MODEL slx_410938a03b86
CONFIG AbsTol = auto
CONFIG EnableMultiTasking = off
CONFIG FixedStep = auto
CONFIG MaxStep = auto
CONFIG MinStep = auto
CONFIG RelTol = 1e-3
CONFIG SampleTimeConstraint = Unconstrained
CONFIG SolverName = ode23s
CONFIG StartTime = 0.0
CONFIG StopTime = 173
BLOCK [Constant] Constant
  Value = max_torque_req
BLOCK [Constant] Constant1
  Value = 0.013
BLOCK [Constant] Constant2
  Value = 0.013
BLOCK [Constant] Constant3
  Value = max_torque_req
BLOCK [FromWorkspace] From Workspace
  VariableName = steering_ang
BLOCK [FromWorkspace] From Workspace2
  VariableName = steering_ang
BLOCK [Gain] Gain
  Gain = 1/M
BLOCK [Gain] Gain1
  Gain = M/4*g
  NameLocation = right
BLOCK [Gain] Gain2
  Gain = M/4*g
  NameLocation = right
BLOCK [Gain] Gain3
  Gain = 8.5/(M/2)
BLOCK [Gain] Gain4
  Gain = 8.5/(M/2)
BLOCK [FromWorkspace] LeftMotorTemp
  VariableName = left_mtr_tmp
BLOCK [SubSystem] MATLAB Function1
  ErrorFcn = Stateflow.Translate.translate
  PermitHierarchicalResolution = ExplicitOnly
  SFBlockType = MATLAB Function
  TreatAsAtomicUnit = on
BLOCK [Demux] MATLAB Function1/ Demux 
  Outputs = 1
BLOCK [S-Function] MATLAB Function1/ SFunction 
  EnableBusSupport = on
  FunctionName = sf_sfun
  PortCounts = [2 2]
  SFcnIsStateOwnerBlock = off
  SFunctionDeploymentMode = off
  Tag = Stateflow S-Function 12
BLOCK [Terminator] MATLAB Function1/ Terminator 
BLOCK [Outport] MATLAB Function1/frr
BLOCK [Inport] MATLAB Function1/prev_wheel_ang_vel
BLOCK [Inport] MATLAB Function1/rolling_coeff
  Port = 2
BLOCK [SubSystem] MATLAB Function2
  ErrorFcn = Stateflow.Translate.translate
  PermitHierarchicalResolution = ExplicitOnly
  SFBlockType = MATLAB Function
  TreatAsAtomicUnit = on
BLOCK [Demux] MATLAB Function2/ Demux 
  Outputs = 1
BLOCK [S-Function] MATLAB Function2/ SFunction 
  EnableBusSupport = on
  FunctionName = sf_sfun
  PortCounts = [2 2]
  SFcnIsStateOwnerBlock = off
  SFunctionDeploymentMode = off
  Tag = Stateflow S-Function 13
BLOCK [Terminator] MATLAB Function2/ Terminator 
BLOCK [Outport] MATLAB Function2/frr
BLOCK [Inport] MATLAB Function2/prev_wheel_ang_vel
BLOCK [Inport] MATLAB Function2/rolling_coeff
  Port = 2
BLOCK [Memory] Memory
BLOCK [Memory] Memory1
BLOCK [Memory] Memory3
  NameLocation = right
BLOCK [FromWorkspace] PedalPercent
  VariableName = pdl_percent
BLOCK [FromWorkspace] PedalPercent1
  VariableName = pdl_percent
BLOCK [SubSystem] Pedal_Based_Torque_Mapping
  ErrorFcn = Stateflow.Translate.translate
  PermitHierarchicalResolution = ExplicitOnly
  SFBlockType = MATLAB Function
  TreatAsAtomicUnit = on
BLOCK [Demux] Pedal_Based_Torque_Mapping/ Demux 
  Outputs = 1
BLOCK [S-Function] Pedal_Based_Torque_Mapping/ SFunction 
  EnableBusSupport = on
  FunctionName = sf_sfun
  PortCounts = [3 3]
  SFcnIsStateOwnerBlock = off
  SFunctionDeploymentMode = off
  Tag = Stateflow S-Function 8
BLOCK [Terminator] Pedal_Based_Torque_Mapping/ Terminator 
BLOCK [Outport] Pedal_Based_Torque_Mapping/T_req_active_diff
BLOCK [Outport] Pedal_Based_Torque_Mapping/T_req_slip_control
  Port = 2
BLOCK [Inport] Pedal_Based_Torque_Mapping/max_torque_req
BLOCK [Inport] Pedal_Based_Torque_Mapping/p_a
  Port = 3
BLOCK [Inport] Pedal_Based_Torque_Mapping/steering_angle
  Port = 2
BLOCK [Product] Product
BLOCK [FromWorkspace] RightMotorTemp
  VariableName = right_mtr_tmp
BLOCK [Scope] Scope
  Floating = off
  NumInputPorts = 1
  ScopeSpecificationString = Simulink.scopes.TimeScopeBlockCfg('CurrentConfiguration', extmgr.ConfigurationSet(extmgr.Configuration('Core','General UI',true),extmgr.Configuration('Core','Source UI',true),extmgr.Configuration('Sources','WiredSimulink',true,'DataLoggingVariableName','ScopeData1'),extmgr.Configuration('Visuals','Time Domain',true,'SerializedDisplays',{struct('MinYLimReal','-128.05151','MaxYLimReal','52.46356','Y...<+1474ch>
BLOCK [Sum] Sum
  Inputs = |+-
BLOCK [Sum] Sum1
  Inputs = |-+
BLOCK [Sum] Sum2
  Inputs = |++
BLOCK [Sum] Sum4
  Inputs = |+-
BLOCK [Sum] Sum5
  Inputs = |++
BLOCK [SubSystem] activeDiff
BLOCK [Constant] activeDiff/Constant
BLOCK [SubSystem] activeDiff/MATLAB Function
  ErrorFcn = Stateflow.Translate.translate
  PermitHierarchicalResolution = ExplicitOnly
  SFBlockType = MATLAB Function
  TreatAsAtomicUnit = on
BLOCK [Demux] activeDiff/MATLAB Function/ Demux 
  Outputs = 1
BLOCK [S-Function] activeDiff/MATLAB Function/ SFunction 
  EnableBusSupport = on
  FunctionName = sf_sfun
  PortCounts = [3 2]
  SFcnIsStateOwnerBlock = off
  SFunctionDeploymentMode = off
  Tag = Stateflow S-Function 9
BLOCK [Terminator] activeDiff/MATLAB Function/ Terminator 
BLOCK [Inport] activeDiff/MATLAB Function/conversion_factor
  Port = 2
BLOCK [Inport] activeDiff/MATLAB Function/inverter_power
BLOCK [Outport] activeDiff/MATLAB Function/motor_RPM
BLOCK [Inport] activeDiff/MATLAB Function/torque_request
  Port = 3
BLOCK [Inport] activeDiff/Pedal Torque
  Port = 3
BLOCK [Inport] activeDiff/Power Limit
  Port = 2
BLOCK [SubSystem] activeDiff/Power_to_torque
  ErrorFcn = Stateflow.Translate.translate
  PermitHierarchicalResolution = ExplicitOnly
  SFBlockType = MATLAB Function
  TreatAsAtomicUnit = on
BLOCK [Demux] activeDiff/Power_to_torque/ Demux 
  Outputs = 1
BLOCK [S-Function] activeDiff/Power_to_torque/ SFunction 
  EnableBusSupport = on
  FunctionName = sf_sfun
  PortCounts = [6 2]
  SFcnIsStateOwnerBlock = off
  SFunctionDeploymentMode = off
  Tag = Stateflow S-Function 7
BLOCK [Terminator] activeDiff/Power_to_torque/ Terminator 
BLOCK [Inport] activeDiff/Power_to_torque/cl
  Port = 4
BLOCK [Inport] activeDiff/Power_to_torque/cr
  Port = 5
BLOCK [Inport] activeDiff/Power_to_torque/left_motor_speed
BLOCK [Outport] activeDiff/Power_to_torque/max_power_to_torque
BLOCK [Inport] activeDiff/Power_to_torque/p_to_t_conversion_factor
  Port = 6
BLOCK [Inport] activeDiff/Power_to_torque/power_KW_input
  Port = 3
BLOCK [Inport] activeDiff/Power_to_torque/right_motor_speed
  Port = 2
BLOCK [Inport] activeDiff/Steering Angle
BLOCK [SubSystem] activeDiff/Steering_Angle_To_Delta
  ErrorFcn = Stateflow.Translate.translate
  PermitHierarchicalResolution = ExplicitOnly
  SFBlockType = MATLAB Function
  TreatAsAtomicUnit = on
BLOCK [Demux] activeDiff/Steering_Angle_To_Delta/ Demux 
  Outputs = 1
BLOCK [S-Function] activeDiff/Steering_Angle_To_Delta/ SFunction 
  EnableBusSupport = on
  FunctionName = sf_sfun
  PortCounts = [3 2]
  SFcnIsStateOwnerBlock = off
  SFunctionDeploymentMode = off
  Tag = Stateflow S-Function 6
BLOCK [Terminator] activeDiff/Steering_Angle_To_Delta/ Terminator 
BLOCK [Inport] activeDiff/Steering_Angle_To_Delta/TRACK_WIDTH_mm
  Port = 2
BLOCK [Inport] activeDiff/Steering_Angle_To_Delta/WHEELBASE_mm
  Port = 3
BLOCK [Outport] activeDiff/Steering_Angle_To_Delta/delta
BLOCK [Inport] activeDiff/Steering_Angle_To_Delta/wheel_angle_deg
BLOCK [Sum] activeDiff/Sum
  Inputs = |++
BLOCK [Sum] activeDiff/Sum1
  Inputs = |+-
BLOCK [Constant] activeDiff/Track_width_mm
  Value = 1100
BLOCK [Constant] activeDiff/Track_width_mm1
  Value = 1550
BLOCK [Constant] activeDiff/conversion_factor
  Value = 9550
BLOCK [Outport] activeDiff/left_active_diff_torque
  Port = 3
BLOCK [Outport] activeDiff/max_power_to_torque
BLOCK [Outport] activeDiff/right_active_diff_torque
  Port = 2
BLOCK [SubSystem] activeDiff/torque_to_send
  ErrorFcn = Stateflow.Translate.translate
  PermitHierarchicalResolution = ExplicitOnly
  SFBlockType = MATLAB Function
  TreatAsAtomicUnit = on
BLOCK [Demux] activeDiff/torque_to_send/ Demux 
  Outputs = 1
BLOCK [S-Function] activeDiff/torque_to_send/ SFunction 
  EnableBusSupport = on
  FunctionName = sf_sfun
  PortCounts = [4 3]
  SFcnIsStateOwnerBlock = off
  SFunctionDeploymentMode = off
  Tag = Stateflow S-Function 5
BLOCK [Terminator] activeDiff/torque_to_send/ Terminator 
BLOCK [Inport] activeDiff/torque_to_send/cl
BLOCK [Inport] activeDiff/torque_to_send/cr
  Port = 2
BLOCK [Outport] activeDiff/torque_to_send/left_computed_torque
BLOCK [Inport] activeDiff/torque_to_send/request_torque
  Port = 3
BLOCK [Outport] activeDiff/torque_to_send/right_computed_torque
  Port = 2
BLOCK [Inport] activeDiff/torque_to_send/torque_lim
  Port = 4
BLOCK [MinMax] clamp1
  Function = max
  Inputs = 2
BLOCK [MinMax] clamp2
  Inputs = 2
BLOCK [MinMax] clamp3
  Function = max
  Inputs = 2
BLOCK [MinMax] clamp4
  Inputs = 2
BLOCK [Gain] drag_f_form
  Gain = 0.5* mass_den * Cd * Af
BLOCK [SubSystem] left_tire_model
BLOCK [Constant] left_tire_model/Constant
  Value = 0
BLOCK [Outport] left_tire_model/F_x_L
  Port = 2
BLOCK [From] left_tire_model/From
  GotoTag = vehicle_v_x
  NameLocation = top
BLOCK [From] left_tire_model/From F_x
  GotoTag = F_x
BLOCK [FromWorkspace] left_tire_model/From Workspace
  SampleTime = -1
  VariableName = recorded_vel
BLOCK [From] left_tire_model/From1
  GotoTag = vehicle_a_x
  NameLocation = top
BLOCK [From] left_tire_model/From2
  GotoTag = slip_ratio
BLOCK [From] left_tire_model/From3
  GotoTag = wheel_ang_v_x
BLOCK [From] left_tire_model/From4
  GotoTag = vehicle_v_x
BLOCK [Gain] left_tire_model/Gain
  Gain = 1/J_w
BLOCK [Gain] left_tire_model/Gain1
  Gain = R
BLOCK [Gain] left_tire_model/Gain2
  Gain = M/4*g
  NameLocation = top
BLOCK [Gain] left_tire_model/Gain4
  Gain = R
  NameLocation = right
BLOCK [Goto] left_tire_model/Goto
  GotoTag = vehicle_a_x
BLOCK [Goto] left_tire_model/Goto1
  GotoTag = vehicle_v_x
BLOCK [Goto] left_tire_model/Goto2
  GotoTag = slip_ratio
BLOCK [Goto] left_tire_model/Goto3
  GotoTag = wheel_ang_v_x
BLOCK [Integrator] left_tire_model/Integrator
BLOCK [Integrator] left_tire_model/Integrator1
BLOCK [MinMax] left_tire_model/Max
  Function = max
  Inputs = 2
BLOCK [SubSystem] left_tire_model/Pacejka Magic Formula
  ErrorFcn = Stateflow.Translate.translate
  NameLocation = top
  PermitHierarchicalResolution = ExplicitOnly
  SFBlockType = MATLAB Function
  TreatAsAtomicUnit = on
BLOCK [Demux] left_tire_model/Pacejka Magic Formula/ Demux 
  Outputs = 1
BLOCK [S-Function] left_tire_model/Pacejka Magic Formula/ SFunction 
  EnableBusSupport = on
  FunctionName = sf_sfun
  Parameters = B,C,D,E
  PortCounts = [1 2]
  SFcnIsStateOwnerBlock = off
  SFunctionDeploymentMode = off
  Tag = Stateflow S-Function 1
BLOCK [Terminator] left_tire_model/Pacejka Magic Formula/ Terminator 
BLOCK [Outport] left_tire_model/Pacejka Magic Formula/friction_coeff
BLOCK [Inport] left_tire_model/Pacejka Magic Formula/lambda
BLOCK [Scope] left_tire_model/Scope
  Floating = off
  NumInputPorts = 2
  ScopeSpecificationString = Simulink.scopes.TimeScopeBlockCfg('CurrentConfiguration', extmgr.ConfigurationSet(extmgr.Configuration('Core','General UI',true),extmgr.Configuration('Core','Source UI',true),extmgr.Configuration('Sources','WiredSimulink',true,'DataLoggingVariableName','ScopeData1'),extmgr.Configuration('Visuals','Time Domain',true,'SerializedDisplays',{struct('MinYLimReal','-96.49476','MaxYLimReal','429.72181','Y...<+1504ch>
BLOCK [Scope] left_tire_model/Slip & friction
  Floating = on
  NumInputPorts = 1
  ScopeSpecificationString = Simulink.scopes.TimeScopeBlockCfg('CurrentConfiguration', extmgr.ConfigurationSet(extmgr.Configuration('Core','General UI',true),extmgr.Configuration('Core','Source UI',true),extmgr.Configuration('Sources','WiredSimulink',true,'DataLoggingVariableName','ScopeData1'),extmgr.Configuration('Visuals','Time Domain',true,'SerializedDisplays',{struct('MinYLimReal','-0.08597','MaxYLimReal','0.7737','YLabe...<+1562ch>
BLOCK [Sum] left_tire_model/Sum
  Inputs = |+-
BLOCK [Inport] left_tire_model/T_in
  Port = 2
BLOCK [Scope] left_tire_model/Torques and speeds
  Floating = on
  NumInputPorts = 1
  ScopeSpecificationString = Simulink.scopes.TimeScopeBlockCfg('CurrentConfiguration', extmgr.ConfigurationSet(extmgr.Configuration('Core','General UI',true,'FigureColor',[0.156862745098039 0.156862745098039 0.156862745098039]),extmgr.Configuration('Core','Source UI',true),extmgr.Configuration('Sources','WiredSimulink',true,'DataLoggingSaveFormat','StructureWithTime','DataLoggingLimitDataPoints',true,'DataLoggingDecimation','...<+2861ch>
BLOCK [Goto] left_tire_model/goto F_x
  GotoTag = F_x
BLOCK [Outport] left_tire_model/slip_ratio
  Port = 4
BLOCK [SubSystem] left_tire_model/slip_ratio_calculation
  ErrorFcn = Stateflow.Translate.translate
  PermitHierarchicalResolution = ExplicitOnly
  SFBlockType = MATLAB Function
  TreatAsAtomicUnit = on
BLOCK [Demux] left_tire_model/slip_ratio_calculation/ Demux 
  Outputs = 1
BLOCK [S-Function] left_tire_model/slip_ratio_calculation/ SFunction 
  EnableBusSupport = on
  FunctionName = sf_sfun
  Parameters = TOL
  PortCounts = [3 2]
  SFcnIsStateOwnerBlock = off
  SFunctionDeploymentMode = off
  Tag = Stateflow S-Function 2
BLOCK [Terminator] left_tire_model/slip_ratio_calculation/ Terminator 
BLOCK [Outport] left_tire_model/slip_ratio_calculation/slip_ratio
BLOCK [Inport] left_tire_model/slip_ratio_calculation/vehicle_a_x
  Port = 3
BLOCK [Inport] left_tire_model/slip_ratio_calculation/vehicle_v_x
  Port = 2
BLOCK [Inport] left_tire_model/slip_ratio_calculation/wheel_v_x
BLOCK [Inport] left_tire_model/vehicle_a_x
BLOCK [Outport] left_tire_model/vehicle_v_x
BLOCK [Outport] left_tire_model/wheel_ang_v_x
  Port = 3
BLOCK [Constant] max_torque
  Value = 90
BLOCK [Constant] max_torque1
  Value = 90
BLOCK [Constant] min_torque
  Value = 0
BLOCK [Constant] min_torque1
  Value = 0
BLOCK [SubSystem] pedal_percent_clamp
  ErrorFcn = Stateflow.Translate.translate
  PermitHierarchicalResolution = ExplicitOnly
  SFBlockType = MATLAB Function
  TreatAsAtomicUnit = on
BLOCK [Demux] pedal_percent_clamp/ Demux 
  Outputs = 1
BLOCK [S-Function] pedal_percent_clamp/ SFunction 
  EnableBusSupport = on
  FunctionName = sf_sfun
  PortCounts = [1 2]
  SFcnIsStateOwnerBlock = off
  SFunctionDeploymentMode = off
  Tag = Stateflow S-Function 10
BLOCK [Terminator] pedal_percent_clamp/ Terminator 
BLOCK [Outport] pedal_percent_clamp/clamped_output
BLOCK [Inport] pedal_percent_clamp/pedal_percent
BLOCK [SubSystem] pedal_percent_clamp1
  ErrorFcn = Stateflow.Translate.translate
  PermitHierarchicalResolution = ExplicitOnly
  SFBlockType = MATLAB Function
  TreatAsAtomicUnit = on
BLOCK [Demux] pedal_percent_clamp1/ Demux 
  Outputs = 1
BLOCK [S-Function] pedal_percent_clamp1/ SFunction 
  EnableBusSupport = on
  FunctionName = sf_sfun
  PortCounts = [1 2]
  SFcnIsStateOwnerBlock = off
  SFunctionDeploymentMode = off
  Tag = Stateflow S-Function 19
BLOCK [Terminator] pedal_percent_clamp1/ Terminator 
BLOCK [Outport] pedal_percent_clamp1/clamped_output
BLOCK [Inport] pedal_percent_clamp1/pedal_percent
BLOCK [SubSystem] powerLimiting
BLOCK [SubSystem] powerLimiting/Avail_Power_From_Temp
  ErrorFcn = Stateflow.Translate.translate
  PermitHierarchicalResolution = ExplicitOnly
  SFBlockType = MATLAB Function
  TreatAsAtomicUnit = on
BLOCK [Demux] powerLimiting/Avail_Power_From_Temp/ Demux 
  Outputs = 1
BLOCK [S-Function] powerLimiting/Avail_Power_From_Temp/ SFunction 
  EnableBusSupport = on
  FunctionName = sf_sfun
  PortCounts = [4 2]
  SFcnIsStateOwnerBlock = off
  SFunctionDeploymentMode = off
  Tag = Stateflow S-Function 3
BLOCK [Terminator] powerLimiting/Avail_Power_From_Temp/ Terminator 
BLOCK [Outport] powerLimiting/Avail_Power_From_Temp/avail_power
BLOCK [Inport] powerLimiting/Avail_Power_From_Temp/curr_power_limit
  Port = 4
BLOCK [Inport] powerLimiting/Avail_Power_From_Temp/decrementing_ratio
BLOCK [Inport] powerLimiting/Avail_Power_From_Temp/max_motor_temp
  Port = 2
BLOCK [Inport] powerLimiting/Avail_Power_From_Temp/motor_cutoff_temp
  Port = 3
BLOCK [Constant] powerLimiting/Car_Power_Limit
  Value = car_power_limit
BLOCK [Constant] powerLimiting/Constant
  Value = cutoff_motor_temp
BLOCK [Constant] powerLimiting/Constant1
  Value = decrement_ratio_PL
BLOCK [Inport] powerLimiting/Left Motor Temp
BLOCK [MinMax] powerLimiting/Max
  Function = max
  Inputs = 2
BLOCK [MinMax] powerLimiting/Max_allowable power
  Inputs = 2
BLOCK [Inport] powerLimiting/Pedal Percent
  Port = 3
BLOCK [Product] powerLimiting/Pedal_Based_Power_Request
BLOCK [Inport] powerLimiting/Right Motor Temp
  Port = 2
BLOCK [MinMax] powerLimiting/full_throttle_limit
  Inputs = 2
BLOCK [Outport] powerLimiting/maxPowerDraw
BLOCK [SubSystem] right_tire_model
BLOCK [Constant] right_tire_model/Constant
  Value = 0
BLOCK [Outport] right_tire_model/F_x_R
BLOCK [From] right_tire_model/From
  GotoTag = vehicle_v_x
  NameLocation = top
BLOCK [From] right_tire_model/From F_x
  GotoTag = F_x
BLOCK [FromWorkspace] right_tire_model/From Workspace
  SampleTime = -1
  VariableName = recorded_vel
BLOCK [From] right_tire_model/From1
  GotoTag = vehicle_a_x
  NameLocation = top
BLOCK [From] right_tire_model/From2
  GotoTag = slip_ratio
BLOCK [From] right_tire_model/From3
  GotoTag = wheel_ang_v_x
BLOCK [From] right_tire_model/From4
  GotoTag = vehicle_v_x
BLOCK [Gain] right_tire_model/Gain
  Gain = 1/J_w
BLOCK [Gain] right_tire_model/Gain1
  Gain = R
BLOCK [Gain] right_tire_model/Gain2
  Gain = M/4*g
  NameLocation = top
BLOCK [Gain] right_tire_model/Gain4
  Gain = R
  NameLocation = right
BLOCK [Goto] right_tire_model/Goto
  GotoTag = vehicle_a_x
BLOCK [Goto] right_tire_model/Goto1
  GotoTag = vehicle_v_x
BLOCK [Goto] right_tire_model/Goto2
  GotoTag = slip_ratio
BLOCK [Goto] right_tire_model/Goto3
  GotoTag = wheel_ang_v_x
BLOCK [Integrator] right_tire_model/Integrator
BLOCK [Integrator] right_tire_model/Integrator1
BLOCK [MinMax] right_tire_model/Max
  Function = max
  Inputs = 2
BLOCK [SubSystem] right_tire_model/Pacejka Magic Formula
  ErrorFcn = Stateflow.Translate.translate
  NameLocation = top
  PermitHierarchicalResolution = ExplicitOnly
  SFBlockType = MATLAB Function
  TreatAsAtomicUnit = on
BLOCK [Demux] right_tire_model/Pacejka Magic Formula/ Demux 
  Outputs = 1
BLOCK [S-Function] right_tire_model/Pacejka Magic Formula/ SFunction 
  EnableBusSupport = on
  FunctionName = sf_sfun
  Parameters = B,C,D,E
  PortCounts = [1 2]
  SFcnIsStateOwnerBlock = off
  SFunctionDeploymentMode = off
  Tag = Stateflow S-Function 4
BLOCK [Terminator] right_tire_model/Pacejka Magic Formula/ Terminator 
BLOCK [Outport] right_tire_model/Pacejka Magic Formula/friction_coeff
BLOCK [Inport] right_tire_model/Pacejka Magic Formula/lambda
BLOCK [Scope] right_tire_model/Scope
  Floating = off
  NumInputPorts = 2
  ScopeSpecificationString = Simulink.scopes.TimeScopeBlockCfg('CurrentConfiguration', extmgr.ConfigurationSet(extmgr.Configuration('Core','General UI',true),extmgr.Configuration('Core','Source UI',true),extmgr.Configuration('Sources','WiredSimulink',true,'DataLoggingVariableName','ScopeData1'),extmgr.Configuration('Visuals','Time Domain',true,'SerializedDisplays',{struct('MinYLimReal','-96.49476','MaxYLimReal','429.72181','Y...<+1475ch>
BLOCK [Scope] right_tire_model/Slip & friction
  Floating = on
  NumInputPorts = 1
  ScopeSpecificationString = Simulink.scopes.TimeScopeBlockCfg('CurrentConfiguration', extmgr.ConfigurationSet(extmgr.Configuration('Core','General UI',true),extmgr.Configuration('Core','Source UI',true),extmgr.Configuration('Sources','WiredSimulink',true,'DataLoggingVariableName','ScopeData1'),extmgr.Configuration('Visuals','Time Domain',true,'SerializedDisplays',{struct('MinYLimReal','-0.08597','MaxYLimReal','0.7737','YLabe...<+1562ch>
BLOCK [Sum] right_tire_model/Sum
  Inputs = |+-
BLOCK [Inport] right_tire_model/T_in
  Port = 2
BLOCK [Scope] right_tire_model/Torques and speeds
  Floating = on
  NumInputPorts = 1
  ScopeSpecificationString = Simulink.scopes.TimeScopeBlockCfg('CurrentConfiguration', extmgr.ConfigurationSet(extmgr.Configuration('Core','General UI',true,'FigureColor',[0.156862745098039 0.156862745098039 0.156862745098039]),extmgr.Configuration('Core','Source UI',true),extmgr.Configuration('Sources','WiredSimulink',true,'DataLoggingSaveFormat','StructureWithTime','DataLoggingLimitDataPoints',true,'DataLoggingDecimation','...<+2861ch>
BLOCK [Goto] right_tire_model/goto F_x
  GotoTag = F_x
BLOCK [Outport] right_tire_model/slip_ratio
  Port = 3
BLOCK [SubSystem] right_tire_model/slip_ratio_calculation
  ErrorFcn = Stateflow.Translate.translate
  PermitHierarchicalResolution = ExplicitOnly
  SFBlockType = MATLAB Function
  TreatAsAtomicUnit = on
BLOCK [Demux] right_tire_model/slip_ratio_calculation/ Demux 
  Outputs = 1
BLOCK [S-Function] right_tire_model/slip_ratio_calculation/ SFunction 
  EnableBusSupport = on
  FunctionName = sf_sfun
  Parameters = TOL
  PortCounts = [3 2]
  SFcnIsStateOwnerBlock = off
  SFunctionDeploymentMode = off
  Tag = Stateflow S-Function 11
BLOCK [Terminator] right_tire_model/slip_ratio_calculation/ Terminator 
BLOCK [Outport] right_tire_model/slip_ratio_calculation/slip_ratio
BLOCK [Inport] right_tire_model/slip_ratio_calculation/vehicle_a_x
  Port = 3
BLOCK [Inport] right_tire_model/slip_ratio_calculation/vehicle_v_x
  Port = 2
BLOCK [Inport] right_tire_model/slip_ratio_calculation/wheel_v_x
BLOCK [Inport] right_tire_model/vehicle_a_x
BLOCK [Outport] right_tire_model/wheel_ang_v_x
  Port = 2
BLOCK [SubSystem] slipController
BLOCK [Constant] slipController/Constant
  Value = ideal_slip
BLOCK [Reference] slipController/Discrete PID Controller (2DOF)  REF=slpidlib/PID Controller (2DOF)
  LibrarySourceBlock = simulink/Discrete/Discrete PID Controller (2DOF)
  SourceBlock = slpidlib/PID Controller (2DOF)
  SourceType = PID 2dof
BLOCK [SubSystem] slipController/MATLAB Function
  ErrorFcn = Stateflow.Translate.translate
  PermitHierarchicalResolution = ExplicitOnly
  SFBlockType = MATLAB Function
  TreatAsAtomicUnit = on
BLOCK [Demux] slipController/MATLAB Function/ Demux 
  Outputs = 1
BLOCK [S-Function] slipController/MATLAB Function/ SFunction 
  EnableBusSupport = on
  FunctionName = sf_sfun
  PortCounts = [3 2]
  SFcnIsStateOwnerBlock = off
  SFunctionDeploymentMode = off
  Tag = Stateflow S-Function 14
BLOCK [Terminator] slipController/MATLAB Function/ Terminator 
BLOCK [Inport] slipController/MATLAB Function/ideal_slip
BLOCK [Inport] slipController/MATLAB Function/left_slip
  Port = 2
BLOCK [Inport] slipController/MATLAB Function/right_slip
  Port = 3
BLOCK [Outport] slipController/MATLAB Function/slip_to_correct
BLOCK [SubSystem] slipController/MATLAB Function1
  ErrorFcn = Stateflow.Translate.translate
  PermitHierarchicalResolution = ExplicitOnly
  SFBlockType = MATLAB Function
  TreatAsAtomicUnit = on
BLOCK [Demux] slipController/MATLAB Function1/ Demux 
  Outputs = 1
BLOCK [S-Function] slipController/MATLAB Function1/ SFunction 
  EnableBusSupport = on
  FunctionName = sf_sfun
  PortCounts = [4 3]
  SFcnIsStateOwnerBlock = off
  SFunctionDeploymentMode = off
  Tag = Stateflow S-Function 15
BLOCK [Terminator] slipController/MATLAB Function1/ Terminator 
BLOCK [Outport] slipController/MATLAB Function1/corr_T_L
BLOCK [Outport] slipController/MATLAB Function1/corr_T_R
  Port = 2
BLOCK [Inport] slipController/MATLAB Function1/left_slip
  Port = 4
BLOCK [Inport] slipController/MATLAB Function1/pid_corr_t
BLOCK [Inport] slipController/MATLAB Function1/right_slip
  Port = 3
BLOCK [Inport] slipController/MATLAB Function1/slip_to_corr
  Port = 2
BLOCK [Scope] slipController/Scope
  Floating = off
  NumInputPorts = 3
  ScopeSpecificationString = Simulink.scopes.TimeScopeBlockCfg('CurrentConfiguration', extmgr.ConfigurationSet(extmgr.Configuration('Core','General UI',true),extmgr.Configuration('Core','Source UI',true),extmgr.Configuration('Sources','WiredSimulink',true,'DataLoggingVariableName','ScopeData1'),extmgr.Configuration('Visuals','Time Domain',true,'SerializedDisplays',{struct('MinYLimReal','-72046.43178','MaxYLimReal','36891.5195...<+1639ch>
BLOCK [Sum] slipController/Sum
  Inputs = |+-
BLOCK [Sum] slipController/Sum1
  Inputs = |+-
BLOCK [Inport] slipController/T_req_slip_control
BLOCK [Constant] slipController/ideal_slip
  Value = ideal_slip
BLOCK [Inport] slipController/left_slip
  Port = 2
BLOCK [Outport] slipController/left_slip_torque
BLOCK [SubSystem] slipController/only_output_if_slip_control_L
  ErrorFcn = Stateflow.Translate.translate
  PermitHierarchicalResolution = ExplicitOnly
  SFBlockType = MATLAB Function
  TreatAsAtomicUnit = on
BLOCK [Demux] slipController/only_output_if_slip_control_L/ Demux 
  Outputs = 1
BLOCK [S-Function] slipController/only_output_if_slip_control_L/ SFunction 
  EnableBusSupport = on
  FunctionName = sf_sfun
  PortCounts = [2 2]
  SFcnIsStateOwnerBlock = off
  SFunctionDeploymentMode = off
  Tag = Stateflow S-Function 16
BLOCK [Terminator] slipController/only_output_if_slip_control_L/ Terminator 
BLOCK [Outport] slipController/only_output_if_slip_control_L/T_input_req_clamp
BLOCK [Inport] slipController/only_output_if_slip_control_L/slip_adjusted_output
  Port = 2
BLOCK [Inport] slipController/only_output_if_slip_control_L/torque_req
BLOCK [SubSystem] slipController/only_output_if_slip_control_R
  ErrorFcn = Stateflow.Translate.translate
  PermitHierarchicalResolution = ExplicitOnly
  SFBlockType = MATLAB Function
  TreatAsAtomicUnit = on
BLOCK [Demux] slipController/only_output_if_slip_control_R/ Demux 
  Outputs = 1
BLOCK [S-Function] slipController/only_output_if_slip_control_R/ SFunction 
  EnableBusSupport = on
  FunctionName = sf_sfun
  PortCounts = [2 2]
  SFcnIsStateOwnerBlock = off
  SFunctionDeploymentMode = off
  Tag = Stateflow S-Function 17
BLOCK [Terminator] slipController/only_output_if_slip_control_R/ Terminator 
BLOCK [Outport] slipController/only_output_if_slip_control_R/T_input_req_clamp
BLOCK [Inport] slipController/only_output_if_slip_control_R/slip_adjusted_output
BLOCK [Inport] slipController/only_output_if_slip_control_R/torque_req
  Port = 2
BLOCK [Inport] slipController/right_slip
  Port = 3
BLOCK [Outport] slipController/right_slip_torque
  Port = 2
BLOCK [SubSystem] slipController1
BLOCK [Constant] slipController1/Constant
  Value = ideal_slip
BLOCK [Reference] slipController1/Discrete PID Controller (2DOF)  REF=slpidlib/PID Controller (2DOF)
  LibrarySourceBlock = simulink/Discrete/Discrete PID Controller (2DOF)
  SourceBlock = slpidlib/PID Controller (2DOF)
  SourceType = PID 2dof
BLOCK [Reference] slipController1/PID Controller (2DOF)  REF=slpidlib/PID Controller (2DOF)
  LibrarySourceBlock = simulink/Continuous/PID Controller (2DOF)
  SourceBlock = slpidlib/PID Controller (2DOF)
  SourceType = PID 2dof
BLOCK [Scope] slipController1/Scope
  Floating = off
  NumInputPorts = 2
  ScopeSpecificationString = Simulink.scopes.TimeScopeBlockCfg('CurrentConfiguration', extmgr.ConfigurationSet(extmgr.Configuration('Core','General UI',true),extmgr.Configuration('Core','Source UI',true),extmgr.Configuration('Sources','WiredSimulink',true,'DataLoggingVariableName','ScopeData1'),extmgr.Configuration('Visuals','Time Domain',true,'SerializedDisplays',{struct('MinYLimReal','-0.0064','MaxYLimReal','0.05627','YLabe...<+1621ch>
BLOCK [Scope] slipController1/Scope1
  Floating = off
  NumInputPorts = 2
  ScopeSpecificationString = Simulink.scopes.TimeScopeBlockCfg('CurrentConfiguration', extmgr.ConfigurationSet(extmgr.Configuration('Core','General UI',true),extmgr.Configuration('Core','Source UI',true),extmgr.Configuration('Sources','WiredSimulink',true,'DataLoggingVariableName','ScopeData1'),extmgr.Configuration('Visuals','Time Domain',true,'SerializedDisplays',{struct('MinYLimReal','-1189341952943218.25','MaxYLimReal','21...<+1594ch>
BLOCK [Sum] slipController1/Sum
  Inputs = |-+
BLOCK [Sum] slipController1/Sum1
  Inputs = +-|
BLOCK [Inport] slipController1/T_req_slip_control
  Port = 3
BLOCK [Inport] slipController1/left_slip
BLOCK [Outport] slipController1/left_slip_torque
BLOCK [SubSystem] slipController1/only_output_if_slip_control_L
  ErrorFcn = Stateflow.Translate.translate
  PermitHierarchicalResolution = ExplicitOnly
  SFBlockType = MATLAB Function
  TreatAsAtomicUnit = on
BLOCK [Demux] slipController1/only_output_if_slip_control_L/ Demux 
  Outputs = 1
BLOCK [S-Function] slipController1/only_output_if_slip_control_L/ SFunction 
  EnableBusSupport = on
  FunctionName = sf_sfun
  PortCounts = [2 2]
  SFcnIsStateOwnerBlock = off
  SFunctionDeploymentMode = off
  Tag = Stateflow S-Function 22
BLOCK [Terminator] slipController1/only_output_if_slip_control_L/ Terminator 
BLOCK [Outport] slipController1/only_output_if_slip_control_L/T_input_req_clamp
BLOCK [Inport] slipController1/only_output_if_slip_control_L/slip_adjusted_output
  Port = 2
BLOCK [Inport] slipController1/only_output_if_slip_control_L/torque_req
BLOCK [SubSystem] slipController1/only_output_if_slip_control_R
  ErrorFcn = Stateflow.Translate.translate
  PermitHierarchicalResolution = ExplicitOnly
  SFBlockType = MATLAB Function
  TreatAsAtomicUnit = on
BLOCK [Demux] slipController1/only_output_if_slip_control_R/ Demux 
  Outputs = 1
BLOCK [S-Function] slipController1/only_output_if_slip_control_R/ SFunction 
  EnableBusSupport = on
  FunctionName = sf_sfun
  PortCounts = [2 2]
  SFcnIsStateOwnerBlock = off
  SFunctionDeploymentMode = off
  Tag = Stateflow S-Function 23
BLOCK [Terminator] slipController1/only_output_if_slip_control_R/ Terminator 
BLOCK [Outport] slipController1/only_output_if_slip_control_R/T_input_req_clamp
BLOCK [Inport] slipController1/only_output_if_slip_control_R/slip_adjusted_output
BLOCK [Inport] slipController1/only_output_if_slip_control_R/torque_req
  Port = 2
BLOCK [Inport] slipController1/right_slip
  Port = 2
BLOCK [Outport] slipController1/right_slip_torque
  Port = 2
BLOCK [Math] square
  Operator = square
LINE Constant1:1 -> MATLAB Function2:2
LINE Constant2:1 -> MATLAB Function1:2
LINE Constant3:1 -> Product:1
LINE Constant:1 -> Pedal_Based_Torque_Mapping:1
LINE From Workspace:1 -> Pedal_Based_Torque_Mapping:2
LINE From Workspace:1 -> Scope:1
LINE From Workspace:1 -> activeDiff:1
LINE Gain1:1 -> Sum4:2
LINE Gain2:1 -> Sum:2
LINE Gain3:1 -> Sum5:2
LINE Gain4:1 -> Sum5:1
LINE Gain:1 -> Sum1:1
LINE LeftMotorTemp:1 -> powerLimiting:1
LINE MATLAB Function1:1 -> Gain1:1
LINE MATLAB Function2:1 -> Gain2:1
LINE Memory1:1 -> MATLAB Function1:1
LINE Memory3:1 -> left_tire_model:1
LINE Memory3:1 -> right_tire_model:1
LINE Memory:1 -> MATLAB Function2:1
LINE PedalPercent1:1 -> pedal_percent_clamp1:1
LINE PedalPercent:1 -> pedal_percent_clamp:1
LINE Pedal_Based_Torque_Mapping:1 -> activeDiff:3
LINE Pedal_Based_Torque_Mapping:2 -> slipController:1
LINE Product:1 -> slipController1:3
LINE RightMotorTemp:1 -> powerLimiting:2
LINE Sum1:1 -> Memory3:1
LINE Sum4:1 -> Gain4:1
LINE Sum5:1 -> Sum1:2
LINE Sum:1 -> Gain3:1
LINE activeDiff/Constant:1 -> activeDiff/Sum1:1
LINE activeDiff/Constant:1 -> activeDiff/Sum:1
LINE activeDiff/MATLAB Function:1 -> activeDiff/Power_to_torque:1
LINE activeDiff/MATLAB Function:1 -> activeDiff/Power_to_torque:2
LINE activeDiff/Pedal Torque:1 -> activeDiff/MATLAB Function:3
LINE activeDiff/Pedal Torque:1 -> activeDiff/torque_to_send:3
LINE activeDiff/Power Limit:1 -> activeDiff/MATLAB Function:1
LINE activeDiff/Power Limit:1 -> activeDiff/Power_to_torque:3
LINE activeDiff/Power_to_torque:1 -> activeDiff/max_power_to_torque:1
LINE activeDiff/Power_to_torque:1 -> activeDiff/torque_to_send:4
LINE activeDiff/Steering Angle:1 -> activeDiff/Steering_Angle_To_Delta:1
LINE activeDiff/Steering_Angle_To_Delta:1 -> activeDiff/Sum1:2
LINE activeDiff/Steering_Angle_To_Delta:1 -> activeDiff/Sum:2
LINE activeDiff/Sum1:1 -> activeDiff/Power_to_torque:5
LINE activeDiff/Sum1:1 -> activeDiff/torque_to_send:2
LINE activeDiff/Sum:1 -> activeDiff/Power_to_torque:4
LINE activeDiff/Sum:1 -> activeDiff/torque_to_send:1
LINE activeDiff/Track_width_mm1:1 -> activeDiff/Steering_Angle_To_Delta:3
LINE activeDiff/Track_width_mm:1 -> activeDiff/Steering_Angle_To_Delta:2
LINE activeDiff/conversion_factor:1 -> activeDiff/MATLAB Function:2
LINE activeDiff/conversion_factor:1 -> activeDiff/Power_to_torque:6
LINE activeDiff/torque_to_send:1 -> activeDiff/left_active_diff_torque:1
LINE activeDiff/torque_to_send:2 -> activeDiff/right_active_diff_torque:1
LINE activeDiff:3 -> Sum2:1
LINE clamp1:1 -> clamp2:2
LINE clamp2:1 -> left_tire_model:2
LINE clamp3:1 -> clamp4:2
LINE clamp4:1 -> right_tire_model:2
LINE drag_f_form:1 -> Gain:1
LINE left_tire_model/Constant:1 -> left_tire_model/Max:1
LINE left_tire_model/From F_x:1 -> left_tire_model/F_x_L:1
LINE left_tire_model/From Workspace:1 -> left_tire_model/Max:2
LINE left_tire_model/From1:1 -> left_tire_model/slip_ratio_calculation:3
LINE left_tire_model/From2:1 -> left_tire_model/slip_ratio:1
LINE left_tire_model/From3:1 -> left_tire_model/wheel_ang_v_x:1
LINE left_tire_model/From4:1 -> left_tire_model/Scope:1
LINE left_tire_model/From:1 -> left_tire_model/slip_ratio_calculation:2
LINE left_tire_model/From:1 -> left_tire_model/vehicle_v_x:1
LINE left_tire_model/Gain1:1 -> left_tire_model/slip_ratio_calculation:1
LINE left_tire_model/Gain2:1 -> left_tire_model/Gain4:1
LINE left_tire_model/Gain2:1 -> left_tire_model/goto F_x:1
LINE left_tire_model/Gain4:1 -> left_tire_model/Sum:2
LINE left_tire_model/Gain:1 -> left_tire_model/Integrator:1
LINE left_tire_model/Integrator1:1 -> left_tire_model/Goto1:1
LINE left_tire_model/Integrator:1 -> left_tire_model/Gain1:1
LINE left_tire_model/Integrator:1 -> left_tire_model/Goto3:1
LINE left_tire_model/Max:1 -> left_tire_model/Scope:2
LINE left_tire_model/Pacejka Magic Formula:1 -> left_tire_model/Gain2:1
LINE left_tire_model/Sum:1 -> left_tire_model/Gain:1
LINE left_tire_model/T_in:1 -> left_tire_model/Sum:1
LINE left_tire_model/slip_ratio_calculation:1 -> left_tire_model/Goto2:1
LINE left_tire_model/slip_ratio_calculation:1 -> left_tire_model/Pacejka Magic Formula:1
LINE left_tire_model/vehicle_a_x:1 -> left_tire_model/Goto:1
LINE left_tire_model/vehicle_a_x:1 -> left_tire_model/Integrator1:1
LINE left_tire_model:1 -> square:1
LINE left_tire_model:2 -> Sum4:1
LINE left_tire_model:3 -> Memory1:1
LINE left_tire_model:4 -> slipController1:1
LINE max_torque1:1 -> clamp4:1
LINE max_torque:1 -> clamp2:1
LINE min_torque1:1 -> clamp3:1
LINE min_torque:1 -> clamp1:1
LINE pedal_percent_clamp1:1 -> Product:2
LINE pedal_percent_clamp:1 -> Pedal_Based_Torque_Mapping:3
LINE pedal_percent_clamp:1 -> powerLimiting:3
LINE powerLimiting/Avail_Power_From_Temp:1 -> powerLimiting/full_throttle_limit:1
LINE powerLimiting/Car_Power_Limit:1 -> powerLimiting/Avail_Power_From_Temp:4
LINE powerLimiting/Car_Power_Limit:1 -> powerLimiting/Pedal_Based_Power_Request:1
LINE powerLimiting/Car_Power_Limit:1 -> powerLimiting/full_throttle_limit:2
LINE powerLimiting/Constant1:1 -> powerLimiting/Avail_Power_From_Temp:1
LINE powerLimiting/Constant:1 -> powerLimiting/Avail_Power_From_Temp:3
LINE powerLimiting/Left Motor Temp:1 -> powerLimiting/Max:1
LINE powerLimiting/Max:1 -> powerLimiting/Avail_Power_From_Temp:2
LINE powerLimiting/Max_allowable power:1 -> powerLimiting/maxPowerDraw:1
LINE powerLimiting/Pedal Percent:1 -> powerLimiting/Pedal_Based_Power_Request:2
LINE powerLimiting/Pedal_Based_Power_Request:1 -> powerLimiting/Max_allowable power:2
LINE powerLimiting/Right Motor Temp:1 -> powerLimiting/Max:2
LINE powerLimiting/full_throttle_limit:1 -> powerLimiting/Max_allowable power:1
LINE powerLimiting:1 -> activeDiff:2
LINE right_tire_model/Constant:1 -> right_tire_model/Max:1
LINE right_tire_model/From F_x:1 -> right_tire_model/F_x_R:1
LINE right_tire_model/From Workspace:1 -> right_tire_model/Max:2
LINE right_tire_model/From1:1 -> right_tire_model/slip_ratio_calculation:3
LINE right_tire_model/From2:1 -> right_tire_model/slip_ratio:1
LINE right_tire_model/From3:1 -> right_tire_model/wheel_ang_v_x:1
LINE right_tire_model/From4:1 -> right_tire_model/Scope:1
LINE right_tire_model/From:1 -> right_tire_model/slip_ratio_calculation:2
LINE right_tire_model/Gain1:1 -> right_tire_model/slip_ratio_calculation:1
LINE right_tire_model/Gain2:1 -> right_tire_model/Gain4:1
LINE right_tire_model/Gain2:1 -> right_tire_model/goto F_x:1
LINE right_tire_model/Gain4:1 -> right_tire_model/Sum:2
LINE right_tire_model/Gain:1 -> right_tire_model/Integrator:1
LINE right_tire_model/Integrator1:1 -> right_tire_model/Goto1:1
LINE right_tire_model/Integrator:1 -> right_tire_model/Gain1:1
LINE right_tire_model/Integrator:1 -> right_tire_model/Goto3:1
LINE right_tire_model/Max:1 -> right_tire_model/Scope:2
LINE right_tire_model/Pacejka Magic Formula:1 -> right_tire_model/Gain2:1
LINE right_tire_model/Sum:1 -> right_tire_model/Gain:1
LINE right_tire_model/T_in:1 -> right_tire_model/Sum:1
LINE right_tire_model/slip_ratio_calculation:1 -> right_tire_model/Goto2:1
LINE right_tire_model/slip_ratio_calculation:1 -> right_tire_model/Pacejka Magic Formula:1
LINE right_tire_model/vehicle_a_x:1 -> right_tire_model/Goto:1
LINE right_tire_model/vehicle_a_x:1 -> right_tire_model/Integrator1:1
LINE right_tire_model:1 -> Sum:1
LINE right_tire_model:2 -> Memory:1
LINE right_tire_model:3 -> slipController1:2
LINE slipController/Constant:1 -> slipController/MATLAB Function:1
LINE slipController/Discrete PID Controller (2DOF):1 -> slipController/MATLAB Function1:1
LINE slipController/MATLAB Function1:1 -> slipController/Sum:1
LINE slipController/MATLAB Function1:2 -> slipController/Sum1:1
LINE slipController/MATLAB Function:1 -> slipController/Discrete PID Controller (2DOF):2
LINE slipController/MATLAB Function:1 -> slipController/MATLAB Function1:2
LINE slipController/Sum1:1 -> slipController/only_output_if_slip_control_R:1
LINE slipController/Sum:1 -> slipController/only_output_if_slip_control_L:2
LINE slipController/T_req_slip_control:1 -> slipController/Sum1:2
LINE slipController/T_req_slip_control:1 -> slipController/Sum:2
LINE slipController/T_req_slip_control:1 -> slipController/only_output_if_slip_control_L:1
LINE slipController/T_req_slip_control:1 -> slipController/only_output_if_slip_control_R:2
LINE slipController/ideal_slip:1 -> slipController/Discrete PID Controller (2DOF):1
LINE slipController/ideal_slip:1 -> slipController/Scope:1
LINE slipController/left_slip:1 -> slipController/MATLAB Function1:4
LINE slipController/left_slip:1 -> slipController/MATLAB Function:2
LINE slipController/left_slip:1 -> slipController/Scope:2
LINE slipController/only_output_if_slip_control_L:1 -> slipController/left_slip_torque:1
LINE slipController/only_output_if_slip_control_R:1 -> slipController/right_slip_torque:1
LINE slipController/right_slip:1 -> slipController/MATLAB Function1:3
LINE slipController/right_slip:1 -> slipController/MATLAB Function:3
LINE slipController/right_slip:1 -> slipController/Scope:3
LINE slipController1/Constant:1 -> slipController1/Discrete PID Controller (2DOF):1
LINE slipController1/Constant:1 -> slipController1/PID Controller (2DOF):1
LINE slipController1/Constant:1 -> slipController1/Scope1:1
LINE slipController1/Constant:1 -> slipController1/Scope:2
LINE slipController1/Discrete PID Controller (2DOF):1 -> slipController1/Sum1:2
LINE slipController1/PID Controller (2DOF):1 -> slipController1/Sum:1
LINE slipController1/Sum1:1 -> slipController1/only_output_if_slip_control_R:1
LINE slipController1/Sum:1 -> slipController1/only_output_if_slip_control_L:2
LINE slipController1/T_req_slip_control:1 -> slipController1/Sum1:1
LINE slipController1/T_req_slip_control:1 -> slipController1/Sum:2
LINE slipController1/T_req_slip_control:1 -> slipController1/only_output_if_slip_control_L:1
LINE slipController1/T_req_slip_control:1 -> slipController1/only_output_if_slip_control_R:2
LINE slipController1/left_slip:1 -> slipController1/PID Controller (2DOF):2
LINE slipController1/left_slip:1 -> slipController1/Scope:1
LINE slipController1/only_output_if_slip_control_L:1 -> slipController1/left_slip_torque:1
LINE slipController1/only_output_if_slip_control_R:1 -> slipController1/right_slip_torque:1
LINE slipController1/right_slip:1 -> slipController1/Discrete PID Controller (2DOF):2
LINE slipController1/right_slip:1 -> slipController1/Scope1:2
LINE slipController1:1 -> clamp1:2
LINE slipController1:2 -> clamp3:2
LINE slipController:1 -> Sum2:2
LINE square:1 -> drag_f_form:1
CHART pedal_percent_clamp states=1 transitions=1
  STATE_LABEL 'eML_blk_kernel()'
  STATE_LABEL 'SCRIPT:\nfunction clamped_output = fcn(pedal_percent)\n\nif pedal_percent < 0\n    clamped_output = 0;\n\nelseif pedal_percent > 1\n    clamped_output = 1;\n\nelse\n    clamped_output = pedal_percent;\n    \nend\n\n'
CHART right_tire_model/slip_ratio_calculation states=1 transitions=1
  STATE_LABEL 'eML_blk_kernel()'
  STATE_LABEL 'SCRIPT:\nfunction slip_ratio = fcn(wheel_v_x, vehicle_v_x, TOL, vehicle_a_x)\n% This is derived from pg. 100 of Rajamani - Vehicle Dynamics and Control\n% (2006)\n\nif vehicle_a_x >= 0\n    slip_ratio = (wheel_v_x- vehicle_v_x)/(wheel_v_x + TOL);\nelse\n    slip_ratio = (wheel_v_x - vehicle_v_x)/(vehicle_v_x + TOL);\nend'
CHART MATLAB Function1 states=1 transitions=1
  STATE_LABEL 'eML_blk_kernel()'
  STATE_LABEL "SCRIPT:\nfunction frr = fcn(prev_wheel_ang_vel, rolling_coeff)\n\n% no physics formula to refer for this however I did this based on\n% intuition... essentially I don't believe rolling resistance should be\n% effecting the friction force on the car if the wheels are not moving\n\nif(prev_wheel_ang_vel <= 0)\n    frr = 0;\nelse\n    frr = rolling_coeff; \nend\n"
CHART MATLAB Function2 states=1 transitions=1
  STATE_LABEL 'eML_blk_kernel()'
  STATE_LABEL "SCRIPT:\nfunction frr = fcn(prev_wheel_ang_vel, rolling_coeff)\n\n% no physics formula to refer for this however I did this based on\n% intuition... essentially I don't believe rolling resistance should be\n% effecting the friction force on the car if the wheels are not moving\n\nif(prev_wheel_ang_vel <= 0)\n    frr = 0;\nelse\n    frr = rolling_coeff; \nend\n"
CHART slipController/MATLAB Function states=1 transitions=1
  STATE_LABEL 'eML_blk_kernel()'
  STATE_LABEL 'SCRIPT:\nfunction slip_to_correct = fcn(ideal_slip, left_slip, right_slip)\n\nerror_left = abs(left_slip - ideal_slip)\nerror_right = abs(right_slip - ideal_slip)\n\nif error_left <= error_right\n    slip_to_correct = left_slip\nelse\n    slip_to_correct = right_slip\nend  '
CHART left_tire_model/Pacejka Magic Formula states=1 transitions=1
  STATE_LABEL 'eML_blk_kernel()'
  STATE_LABEL 'SCRIPT:\nfunction friction_coeff = fcn(lambda, B, C, D, E)\n\nfriction_coeff = D*sin(C*atan(B*lambda -  E*(B*lambda - atan(B*lambda))));'
CHART slipController/MATLAB Function1 states=1 transitions=1
  STATE_LABEL 'eML_blk_kernel()'
  STATE_LABEL 'SCRIPT:\nfunction [corr_T_L, corr_T_R] = fcn(pid_corr_t, ...\n    slip_to_corr, right_slip,left_slip)\n\n% This function is there to route the PID correction based on which motor\n% ie. wheel the correction is for. The other wheel should recieve a 0\n% correction\n\ncorr_T_L = 0;\ncorr_T_R = 0; \n\nif(slip_to_corr == left_slip)\n    corr_T_L = pid_corr_t\nelseif (slip_to_corr == right_slip)\n    corr_T_R = pid_...<+11ch>'
CHART slipController/only_output_if_slip_control_L states=1 transitions=1
  STATE_LABEL 'eML_blk_kernel()'
  STATE_LABEL 'SCRIPT:\nfunction T_input_req_clamp = fcn(torque_req, slip_adjusted_output)\n\nif torque_req == 0\n    T_input_req_clamp = slip_adjusted_output;\nelse\n    T_input_req_clamp = 0;\nend '
CHART slipController/only_output_if_slip_control_R states=1 transitions=1
  STATE_LABEL 'eML_blk_kernel()'
  STATE_LABEL 'SCRIPT:\nfunction T_input_req_clamp = fcn(slip_adjusted_output, torque_req)\n\nif torque_req == 0\n    T_input_req_clamp = slip_adjusted_output;\nelse\n    T_input_req_clamp = 0;\nend '
CHART pedal_percent_clamp1 states=1 transitions=1
  STATE_LABEL 'eML_blk_kernel()'
  STATE_LABEL 'SCRIPT:\nfunction clamped_output = fcn(pedal_percent)\n\nif pedal_percent < 0\n    clamped_output = 0;\n\nelseif pedal_percent > 1\n    clamped_output = 1;\n\nelse\n    clamped_output = pedal_percent;\n    \nend\n\n'
CHART slipController1/only_output_if_slip_control_L states=1 transitions=1
  STATE_LABEL 'eML_blk_kernel()'
  STATE_LABEL 'SCRIPT:\nfunction T_input_req_clamp = fcn(torque_req, slip_adjusted_output)\n\nif torque_req == 0\n    T_input_req_clamp = 0;\nelse\n    T_input_req_clamp = slip_adjusted_output;\nend '
CHART slipController1/only_output_if_slip_control_R states=1 transitions=1
  STATE_LABEL 'eML_blk_kernel()'
  STATE_LABEL 'SCRIPT:\nfunction T_input_req_clamp = fcn(slip_adjusted_output, torque_req)\n\n\nif torque_req == 0\n    T_input_req_clamp = 0;\nelse\n    T_input_req_clamp = slip_adjusted_output;\nend '
CHART left_tire_model/slip_ratio_calculation states=1 transitions=1
  STATE_LABEL 'eML_blk_kernel()'
  STATE_LABEL 'SCRIPT:\nfunction slip_ratio = fcn(wheel_v_x, vehicle_v_x, TOL, vehicle_a_x)\n% This is derived from pg. 100 of Rajamani - Vehicle Dynamics and Control\n% (2006)\n\nif vehicle_a_x >= 0\n    slip_ratio = (wheel_v_x- vehicle_v_x)/(wheel_v_x + TOL);\nelse\n    slip_ratio = (wheel_v_x - vehicle_v_x)/(vehicle_v_x + TOL);\nend'
CHART powerLimiting/Avail_Power_From_Temp states=1 transitions=1
  STATE_LABEL 'eML_blk_kernel()'
  STATE_LABEL 'SCRIPT:\nfunction avail_power = fcn( decrementing_ratio,max_motor_temp, ...\n    motor_cutoff_temp, curr_power_limit)\n\navail_power = curr_power_limit;\n\nif (max_motor_temp - motor_cutoff_temp) >= 30.0\n    avail_power = 0.0;\nelseif max_motor_temp > motor_cutoff_temp\n    avail_power = curr_power_limit - ...\n    (max_motor_temp - motor_cutoff_temp) * ...\n    decrementing_ratio;\nend\n\n'
CHART right_tire_model/Pacejka Magic Formula states=1 transitions=1
  STATE_LABEL 'eML_blk_kernel()'
  STATE_LABEL 'SCRIPT:\nfunction friction_coeff = fcn(lambda, B, C, D, E)\n\nfriction_coeff = D*sin(C*atan(B*lambda -  E*(B*lambda - atan(B*lambda))));'
CHART activeDiff/torque_to_send states=1 transitions=1
  STATE_LABEL 'eML_blk_kernel()'
  STATE_LABEL 'SCRIPT:\n% this block should theoritically not do anything as of now because of the\n% way motor speed was calculate (the output of maxPower_to_Torque is going\n% to be requested torque as of now)\n\nfunction [left_computed_torque, right_computed_torque]...\n= fcn(cl, cr, request_torque, torque_lim)\n\n% will be the same for now \ntorque_left_nm = request_torque * cl; \ntorque_right_nm = request_torque * cr...<+532ch>'
CHART activeDiff/Steering_Angle_To_Delta states=1 transitions=1
  STATE_LABEL 'eML_blk_kernel()'
  STATE_LABEL 'SCRIPT:\nfunction delta = fcn(wheel_angle_deg, TRACK_WIDTH_mm, WHEELBASE_mm)\n\ndelta = TRACK_WIDTH_mm * tan(deg2rad(wheel_angle_deg)) / (2 * WHEELBASE_mm);\n'
CHART activeDiff/Power_to_torque states=1 transitions=1
  STATE_LABEL 'eML_blk_kernel()'
  STATE_LABEL 'SCRIPT:\nfunction max_power_to_torque = fcn(left_motor_speed, right_motor_speed,power_KW_input, ...\n    cl,cr, p_to_t_conversion_factor)\n\n% taken directly from code .. standard motor torque charac eqn assumes\n% torque is equally distributed between left and right wheel\n\n% since our power limit torque is calcuated using requested torque if we\n% use the main power to torque formula that we use in cod...<+553ch>'
CHART Pedal_Based_Torque_Mapping states=1 transitions=1
  STATE_LABEL 'eML_blk_kernel()'
  STATE_LABEL 'SCRIPT:\nfunction [T_req_active_diff, T_req_slip_control]= ...\nfcn(max_torque_req,steering_angle, p_a)\n\n\n\nif (-10.0 <= steering_angle && steering_angle <= 10.0)\n    T_req_active_diff = 0;\n    T_req_slip_control = max_torque_req* p_a;\nelse \n    T_req_active_diff = max_torque_req * p_a;\n    T_req_slip_control = 0;\nend \n'
CHART activeDiff/MATLAB Function states=1 transitions=1
  STATE_LABEL 'eML_blk_kernel()'
  STATE_LABEL 'SCRIPT:\nfunction motor_RPM = fcn(inverter_power, conversion_factor, torque_request)\n\n% kinda sus calculation but we need a way to calculate motor speed from\n% torque... decided to use W = 9550 * P in KW /T N in rpm \n% problem is the power_to_torque function just calculates using the same\n% formula so essentially it will go back to the torque request \n\nmotor_RPM = (inverter_power * conversion_facto...<+33ch>'
CHART  states=0 transitions=0
CHART  states=0 transitions=0
CHART  states=0 transitions=0
CHART  states=0 transitions=0
CHART  states=0 transitions=0
CHART  states=0 transitions=0
CHART  states=0 transitions=0
CHART  states=0 transitions=0
CHART  states=0 transitions=0
CHART  states=0 transitions=0
CHART  states=0 transitions=0
CHART  states=0 transitions=0
CHART  states=0 transitions=0
CHART  states=0 transitions=0
CHART  states=0 transitions=0
CHART  states=0 transitions=0
CHART  states=0 transitions=0
CHART  states=0 transitions=0
CHART  states=0 transitions=0
CHART  states=0 transitions=0
